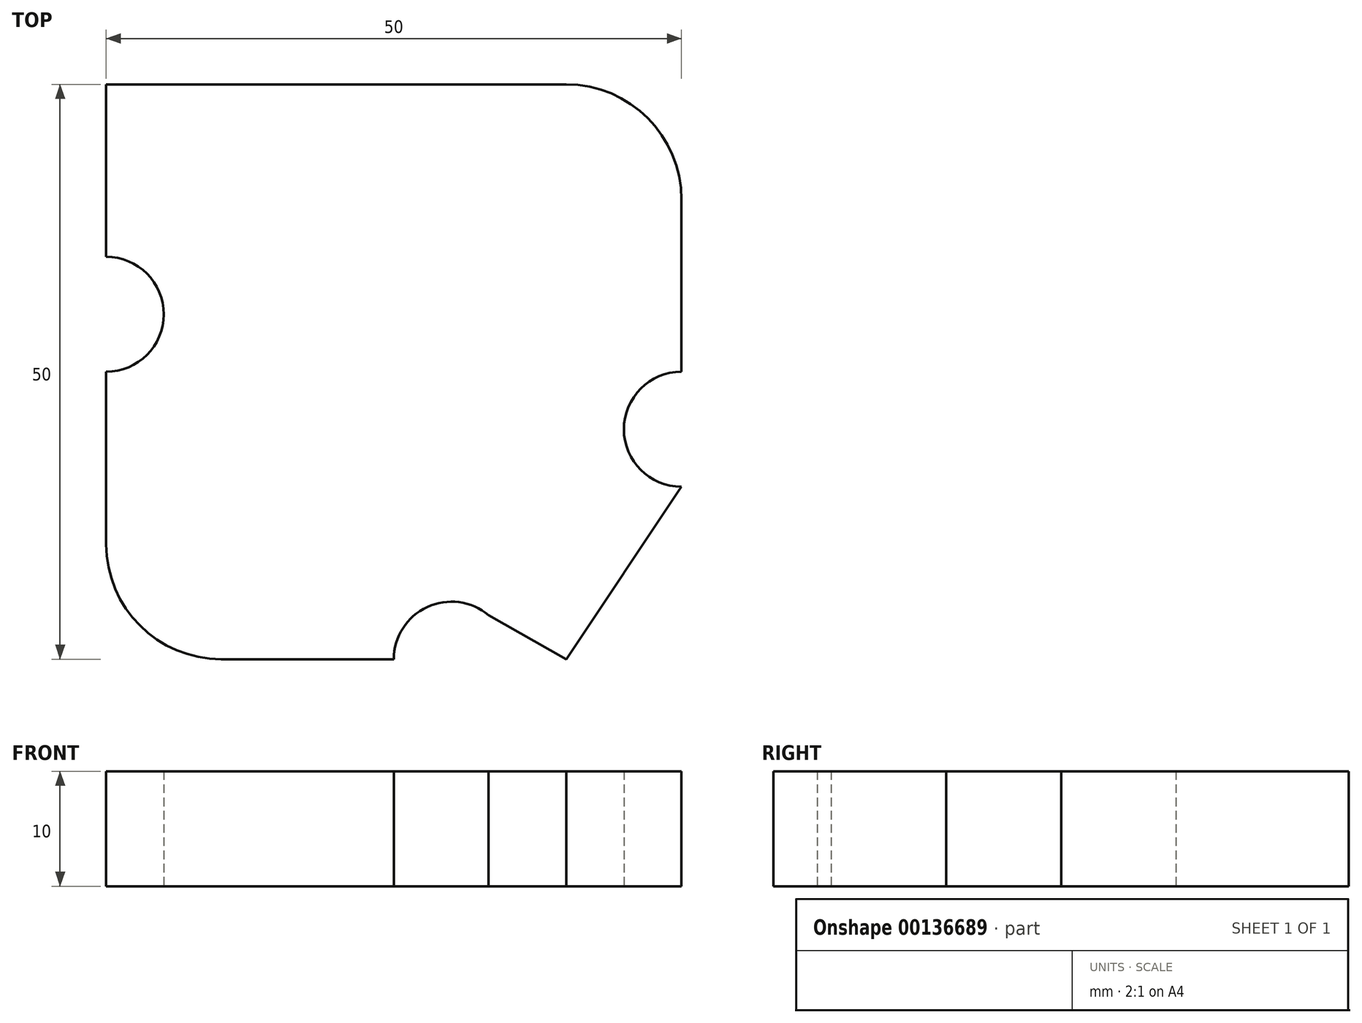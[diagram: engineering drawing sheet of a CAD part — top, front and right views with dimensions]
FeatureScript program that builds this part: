
annotation { "Feature Type Name" : "Feature", "Feature Type Description" : "" }
export const myFeature = defineFeature(function(context is Context, id is Id, definition is map)
    precondition{}
    {
        {
            var Q0;
            Q0=qCreatedBy(makeId("Top.planeOp"),FACE);
            var sketch = newSketch(context, id + "F0", { "sketchPlane" : qUnion([Q0])});
            skLineSegment(sketch, "E0.bottom", {"start": v(15, 25) * mm, "end": v(-25, 25) * mm});
            skLineSegment(sketch, "E0.top", {"start": v(0, -25) * mm, "end": v(-15, -25) * mm});
            skLineSegment(sketch, "E0.left", {"start": v(25, 15) * mm, "end": v(25, 0) * mm});
            skLineSegment(sketch, "E0.right", {"start": v(-25, 25) * mm, "end": v(-25, 10) * mm});
            skPoint(sketch, "E0.middle", {"position": v(0, 0) * mm});
            skArc(sketch, "E1", {"start": v(-25, 0) * mm, "mid": v(-20, 5) * mm, "end": v(-25, 10) * mm});
            skArc(sketch, "E2.filletArc", {"start": v(25, 15) * mm, "mid": v(22.07, 22.07) * mm, "end": v(15, 25) * mm});
            skArc(sketch, "E3", {"start": v(25, 0) * mm, "mid": v(20, -5) * mm, "end": v(25, -10) * mm});
            skArc(sketch, "E4.filletArc", {"start": v(-25, -15) * mm, "mid": v(-22.07, -22.07) * mm, "end": v(-15, -25) * mm});
            skArc(sketch, "E5", {"start": v(8.23, -21.18) * mm, "mid": v(2.9, -20.46) * mm, "end": v(0, -25) * mm});
            skLineSegment(sketch, "E6", {"start": v(6.6, -20.26) * mm, "end": v(15, -25) * mm});
            skLineSegment(sketch, "E7", {"start": v(15, -25) * mm, "end": v(25, -10) * mm});
            skPoint(sketch, "E8.orphan", {"position": v(25, -25) * mm});
            skLineSegment(sketch, "E9.trimOffspring", {"start": v(-25, 0) * mm, "end": v(-25, -15) * mm});
            skSolve(sketch);
        }
        {
            var Q0;
            Q0=makeQuery(id+"F0.imprint","IMPRINT",FACE,{"disambiguationData":[TD([[makeQuery(id+"F0.imprint","IMPRINT",EDGE,{"derivedFrom":sQuery(id+"F0.wireOp",EDGE,"E0.bottom")}),1.0]])]});
            extrude(context, id + "F1", {"entities" : qUnion([Q0]), "depth" : 10 * mm});
        }
    });
